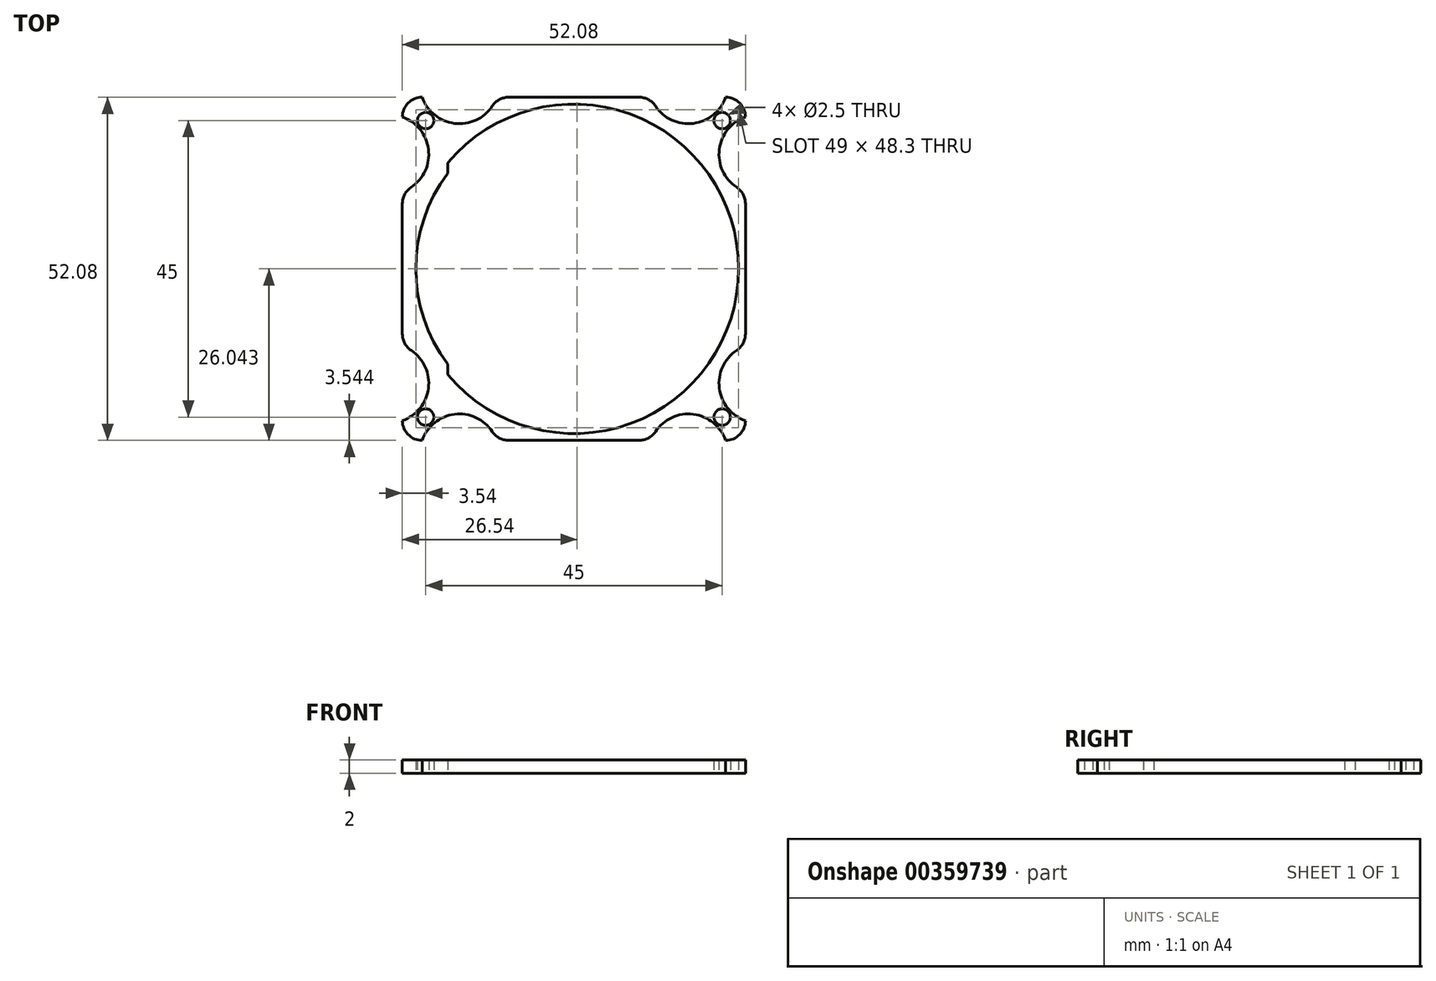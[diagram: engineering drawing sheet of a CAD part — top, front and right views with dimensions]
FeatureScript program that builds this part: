
annotation { "Feature Type Name" : "Feature", "Feature Type Description" : "" }
export const myFeature = defineFeature(function(context is Context, id is Id, definition is map)
    precondition{}
    {
        {
            var Q0;
            Q0=qCreatedBy(makeId("Top.planeOp"),FACE);
            var sketch = newSketch(context, id + "F0", { "sketchPlane" : qUnion([Q0])});
            skLineSegment(sketch, "E0", {"start": v(5.45, 22.77) * mm, "end": v(-46.63, -29.3) * mm, "construction": true});
            skLineSegment(sketch, "E1", {"start": v(-46.63, 22.77) * mm, "end": v(5.45, -29.3) * mm, "construction": true});
            skLineSegment(sketch, "E2", {"start": v(-43.09, 19.23) * mm, "end": v(-43.09, -25.77) * mm, "construction": true});
            skLineSegment(sketch, "E3", {"start": v(-43.09, -25.77) * mm, "end": v(1.91, -25.77) * mm, "construction": true});
            skLineSegment(sketch, "E4", {"start": v(1.91, -25.77) * mm, "end": v(1.91, 19.23) * mm, "construction": true});
            skLineSegment(sketch, "E5", {"start": v(1.91, 19.23) * mm, "end": v(-43.09, 19.23) * mm, "construction": true});
            skCircle(sketch, "E6", {"center": v(-43.09, 19.23) * mm, "radius": 1.25 * mm});
            skCircle(sketch, "E7", {"center": v(1.91, 19.23) * mm, "radius": 1.25 * mm});
            skCircle(sketch, "E8", {"center": v(1.91, -25.77) * mm, "radius": 1.25 * mm});
            skCircle(sketch, "E9", {"center": v(-43.09, -25.77) * mm, "radius": 1.25 * mm});
            skCircle(sketch, "E10", {"center": v(-20.59, -3.27) * mm, "radius": 25 * mm});
            skArc(sketch, "E11", {"start": v(-39.74, 11.2) * mm, "mid": v(-44.59, -3.27) * mm, "end": v(-39.74, -17.73) * mm});
            skArc(sketch, "E12.trimOffspring", {"start": v(-1.44, -17.73) * mm, "mid": v(3.41, -3.27) * mm, "end": v(-1.44, 11.2) * mm});
            skLineSegment(sketch, "E13", {"start": v(-39.74, 13.19) * mm, "end": v(-39.74, 11.2) * mm});
            skPoint(sketch, "E14.MirrorCS.start.orphan", {"position": v(-39.6, 12.65) * mm});
            skLineSegment(sketch, "E15", {"start": v(-1.44, 13.19) * mm, "end": v(-1.44, 11.2) * mm});
            skPoint(sketch, "E16.trimOffspring.end.orphan", {"position": v(-2.49, 12.65) * mm});
            skLineSegment(sketch, "E17", {"start": v(-39.74, -19.72) * mm, "end": v(-39.74, -17.73) * mm});
            skLineSegment(sketch, "E18", {"start": v(-1.44, -19.72) * mm, "end": v(-1.44, -17.73) * mm});
            skPoint(sketch, "E19.trimOffspring.end.orphan", {"position": v(-2.49, -19.35) * mm});
            skPoint(sketch, "E20.MirrorCS.start.orphan", {"position": v(-39.6, -19.35) * mm});
            skLineSegment(sketch, "E21.bottom", {"start": v(-10.7, 22.77) * mm, "end": v(-30.48, 22.77) * mm});
            skLineSegment(sketch, "E21.top", {"start": v(-10.7, -29.3) * mm, "end": v(-30.48, -29.3) * mm});
            skLineSegment(sketch, "E21.left", {"start": v(5.45, 6.62) * mm, "end": v(5.45, -13.15) * mm});
            skLineSegment(sketch, "E21.right", {"start": v(-46.63, 6.62) * mm, "end": v(-46.63, -13.15) * mm});
            skLineSegment(sketch, "E22", {"start": v(-20.59, -3.27) * mm, "end": v(-20.59, 22.77) * mm, "construction": true});
            skLineSegment(sketch, "E23", {"start": v(-20.59, -3.27) * mm, "end": v(-20.59, -29.3) * mm, "construction": true});
            skLineSegment(sketch, "E24", {"start": v(-20.59, -3.27) * mm, "end": v(5.45, -3.27) * mm, "construction": true});
            skLineSegment(sketch, "E25", {"start": v(-20.59, -3.27) * mm, "end": v(-46.63, -3.27) * mm, "construction": true});
            skPoint(sketch, "E26.visualSharp", {"position": v(-46.63, 22.77) * mm});
            skArc(sketch, "E26.filletArc", {"start": v(-43.63, 22.77) * mm, "mid": v(-45.75, 21.9) * mm, "end": v(-46.63, 19.77) * mm});
            skPoint(sketch, "E27.visualSharp", {"position": v(5.45, 22.77) * mm});
            skArc(sketch, "E27.filletArc", {"start": v(5.45, 19.77) * mm, "mid": v(4.57, 21.9) * mm, "end": v(2.45, 22.77) * mm});
            skPoint(sketch, "E28.visualSharp", {"position": v(5.45, -29.3) * mm});
            skArc(sketch, "E28.filletArc", {"start": v(2.45, -29.3) * mm, "mid": v(4.57, -28.43) * mm, "end": v(5.45, -26.3) * mm});
            skPoint(sketch, "E29.visualSharp", {"position": v(-46.63, -29.3) * mm});
            skArc(sketch, "E29.filletArc", {"start": v(-46.63, -26.3) * mm, "mid": v(-45.75, -28.43) * mm, "end": v(-43.63, -29.3) * mm});
            skArc(sketch, "E30", {"start": v(5.45, 19.77) * mm, "mid": v(1.49, 14.86) * mm, "end": v(4.11, 9.12) * mm});
            skArc(sketch, "E31.MirrorCS", {"start": v(5.45, -26.3) * mm, "mid": v(1.44, -20.64) * mm, "end": v(5.45, -14.98) * mm});
            skArc(sketch, "E32.MirrorCS", {"start": v(5.45, -26.3) * mm, "mid": v(1.49, -21.4) * mm, "end": v(4.11, -15.65) * mm});
            skArc(sketch, "E33.MirrorCS", {"start": v(2.45, 22.77) * mm, "mid": v(-2.46, 18.8) * mm, "end": v(-8.2, 21.44) * mm});
            skArc(sketch, "E34.MirrorCS", {"start": v(-43.63, -29.3) * mm, "mid": v(-38.71, -25.34) * mm, "end": v(-32.97, -27.97) * mm});
            skArc(sketch, "E35.MirrorCS", {"start": v(-46.63, -26.3) * mm, "mid": v(-42.66, -21.4) * mm, "end": v(-45.3, -15.65) * mm});
            skArc(sketch, "E36.MirrorCS", {"start": v(2.45, -29.3) * mm, "mid": v(-2.46, -25.34) * mm, "end": v(-8.2, -27.97) * mm});
            skArc(sketch, "E37.MirrorCS", {"start": v(-46.63, 19.77) * mm, "mid": v(-42.66, 14.86) * mm, "end": v(-45.3, 9.12) * mm});
            skArc(sketch, "E38.MirrorCS", {"start": v(-43.63, 22.77) * mm, "mid": v(-38.71, 18.8) * mm, "end": v(-32.97, 21.44) * mm});
            skPoint(sketch, "E39.visualSharp", {"position": v(-32.3, 22.77) * mm});
            skArc(sketch, "E39.filletArc", {"start": v(-30.48, 22.77) * mm, "mid": v(-31.9, 22.42) * mm, "end": v(-32.97, 21.44) * mm});
            skPoint(sketch, "E40.visualSharp", {"position": v(-8.87, 22.77) * mm});
            skArc(sketch, "E40.filletArc", {"start": v(-8.2, 21.44) * mm, "mid": v(-9.29, 22.42) * mm, "end": v(-10.7, 22.77) * mm});
            skPoint(sketch, "E41.visualSharp", {"position": v(5.45, 8.45) * mm});
            skArc(sketch, "E41.filletArc", {"start": v(5.45, 6.62) * mm, "mid": v(5.1, 8.04) * mm, "end": v(4.11, 9.12) * mm});
            skPoint(sketch, "E42.visualSharp", {"position": v(5.45, -14.98) * mm});
            skArc(sketch, "E42.filletArc", {"start": v(4.11, -15.65) * mm, "mid": v(5.1, -14.57) * mm, "end": v(5.45, -13.15) * mm});
            skPoint(sketch, "E43.visualSharp", {"position": v(-8.87, -29.3) * mm});
            skArc(sketch, "E43.filletArc", {"start": v(-10.7, -29.3) * mm, "mid": v(-9.29, -28.95) * mm, "end": v(-8.2, -27.97) * mm});
            skPoint(sketch, "E44.visualSharp", {"position": v(-32.3, -29.3) * mm});
            skArc(sketch, "E44.filletArc", {"start": v(-32.97, -27.97) * mm, "mid": v(-31.9, -28.95) * mm, "end": v(-30.48, -29.3) * mm});
            skPoint(sketch, "E45.visualSharp", {"position": v(-46.63, -14.98) * mm});
            skArc(sketch, "E45.filletArc", {"start": v(-46.63, -13.15) * mm, "mid": v(-46.27, -14.57) * mm, "end": v(-45.3, -15.65) * mm});
            skPoint(sketch, "E46.visualSharp", {"position": v(-46.63, 8.45) * mm});
            skArc(sketch, "E46.filletArc", {"start": v(-45.3, 9.12) * mm, "mid": v(-46.27, 8.04) * mm, "end": v(-46.63, 6.62) * mm});
            skSolve(sketch);
        }
        {
            var Q0;
            Q0=makeQuery(id+"F0.imprint","IMPRINT",FACE,{"disambiguationData":[TD([[makeQuery(id+"F0.imprint","IMPRINT",EDGE,{"derivedFrom":sQuery(id+"F0.wireOp",EDGE,"E11")}),-1.0]])]});
            var Q1;
            Q1=makeQuery(id+"F0.imprint","IMPRINT",FACE,{"disambiguationData":[TD([[makeQuery(id+"F0.imprint","IMPRINT",EDGE,{"derivedFrom":sQuery(id+"F0.wireOp",EDGE,"E6")}),-1.0]])]});
            extrude(context, id + "F1", {"entities" : qUnion([Q0, Q1]), "depth" : 2 * mm});
        }
    });
